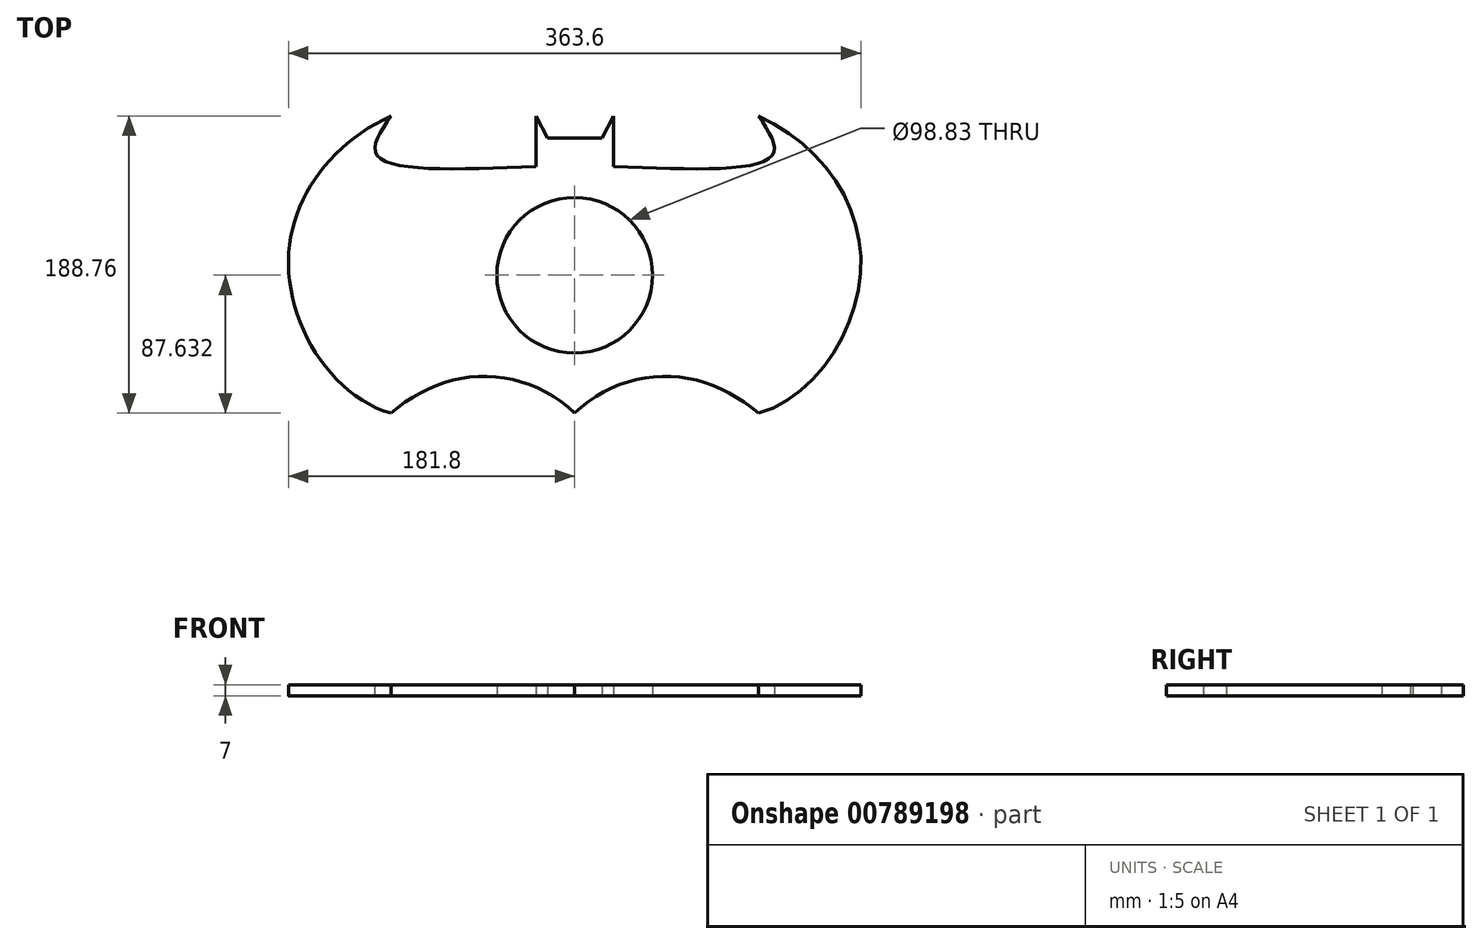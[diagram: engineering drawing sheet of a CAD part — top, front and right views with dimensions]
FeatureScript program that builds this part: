
annotation { "Feature Type Name" : "Feature", "Feature Type Description" : "" }
export const myFeature = defineFeature(function(context is Context, id is Id, definition is map)
    precondition{}
    {
        {
            var Q0;
            Q0=qCreatedBy(makeId("Top.planeOp"),FACE);
            var sketch = newSketch(context, id + "F0", { "sketchPlane" : qUnion([Q0])});
            skLineSegment(sketch, "E0.left", {"start": v(0, 94.38) * mm, "end": v(0, 96.91) * mm});
            skFitSpline(sketch, "E1", {"points": [v(65.07, 0) * mm, v(0, 94.38) * mm, v(65.07, 188.76) * mm], "startDerivative": vector(-222.58, 63) * mm, "endDerivative": vector(236.14, 108.32) * mm});
            skFitSpline(sketch, "E2", {"points": [v(65.07, 188.76) * mm, v(56.02, 164.18) * mm, v(157.16, 156.84) * mm], "startDerivative": vector(-57.05, -83.37) * mm, "endDerivative": vector(212, 9.43) * mm});
            skLineSegment(sketch, "E3", {"start": v(157.16, 156.84) * mm, "end": v(157.16, 188.76) * mm});
            skLineSegment(sketch, "E4", {"start": v(157.16, 188.76) * mm, "end": v(164.5, 174.92) * mm});
            skPoint(sketch, "E5.end.orphan", {"position": v(205.75, 156.84) * mm});
            skLineSegment(sketch, "E6", {"start": v(164.5, 174.92) * mm, "end": v(181.8, 174.92) * mm});
            skLineSegment(sketch, "E7", {"start": v(181.8, 175.26) * mm, "end": v(181.8, 0) * mm, "construction": true});
            skFitSpline(sketch, "E8", {"points": [v(65.07, 0) * mm, v(123.26, 23.5) * mm, v(181.8, 0) * mm], "startDerivative": vector(101.7, 86.73) * mm, "endDerivative": vector(94.92, -93.51) * mm});
            skPoint(sketch, "E9.orphan", {"position": v(0, 188.76) * mm});
            skPoint(sketch, "E10.orphan", {"position": v(0, 0) * mm});
            skFitSpline(sketch, "E11.MirrorCS", {"points": [v(298.52, 188.76) * mm, v(307.56, 164.18) * mm, v(206.42, 156.84) * mm], "startDerivative": vector(57.05, -83.37) * mm, "endDerivative": vector(-212, 9.43) * mm});
            skLineSegment(sketch, "E12.MirrorCS", {"start": v(199.07, 174.92) * mm, "end": v(181.8, 174.92) * mm});
            skLineSegment(sketch, "E13.MirrorCS", {"start": v(206.42, 188.76) * mm, "end": v(199.07, 174.92) * mm});
            skLineSegment(sketch, "E14.MirrorCS", {"start": v(206.42, 156.84) * mm, "end": v(206.42, 188.76) * mm});
            skFitSpline(sketch, "E15.MirrorCS", {"points": [v(298.52, 0) * mm, v(363.58, 94.38) * mm, v(298.52, 188.76) * mm], "startDerivative": vector(222.58, 63) * mm, "endDerivative": vector(-236.14, 108.32) * mm});
            skFitSpline(sketch, "E16.MirrorCS", {"points": [v(298.52, 0) * mm, v(240.32, 23.5) * mm, v(181.8, 0) * mm], "startDerivative": vector(-101.7, 86.73) * mm, "endDerivative": vector(-94.92, -93.51) * mm});
            skPoint(sketch, "E17.center.orphan", {"position": v(181.8, 87.63) * mm});
            skCircle(sketch, "E18", {"center": v(181.8, 87.63) * mm, "radius": 49.42 * mm});
            skSolve(sketch);
        }
        {
            var Q0;
            Q0 = qSketchRegion(id + "F0", true);
            var Q1;
            {var subQ1=sQuery(id+"F0.wireOp",EDGE,"E0.left");Q1=makeQuery(id+"F0.imprint","IMPRINT",FACE,{"disambiguationData":[TD([[makeQuery(id+"F0.imprint","IMPRINT",EDGE,{"derivedFrom":subQ1}),-1.0]])]});}
            extrude(context, id + "F1", {"entities" : qUnion([Q0, Q1]), "depth" : 7 * mm, "offsetDistance" : 25.4 * mm});
        }
    });
